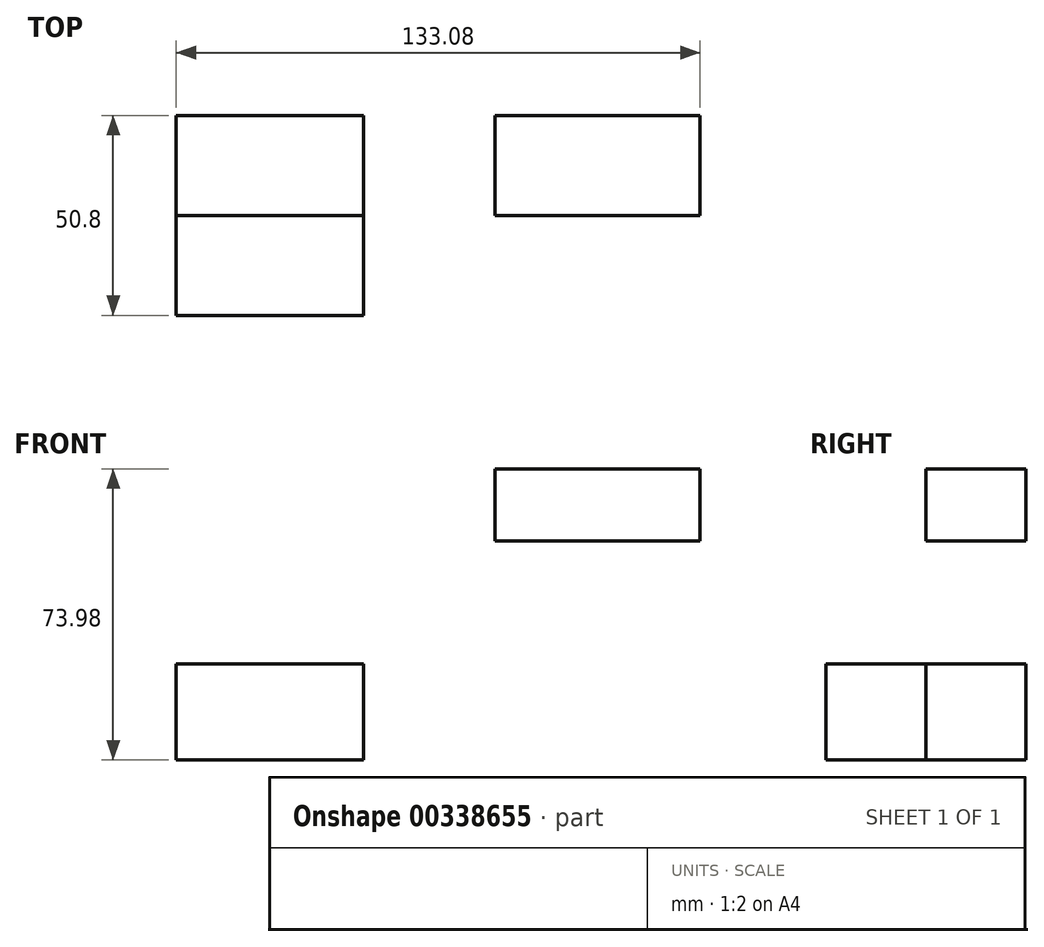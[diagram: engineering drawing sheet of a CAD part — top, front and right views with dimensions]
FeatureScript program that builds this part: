
annotation { "Feature Type Name" : "Feature", "Feature Type Description" : "" }
export const myFeature = defineFeature(function(context is Context, id is Id, definition is map)
    precondition{}
    {
        {
            var Q0;
            Q0=qCreatedBy(makeId("Front.planeOp"),FACE);
            var sketch = newSketch(context, id + "F0", { "sketchPlane" : qUnion([Q0])});
            skLineSegment(sketch, "E0.bottom", {"start": v(23.78, -12.24) * mm, "end": v(-23.78, -12.24) * mm});
            skLineSegment(sketch, "E0.top", {"start": v(23.78, 12.24) * mm, "end": v(-23.78, 12.24) * mm});
            skLineSegment(sketch, "E0.left", {"start": v(23.78, -12.24) * mm, "end": v(23.78, 12.24) * mm});
            skLineSegment(sketch, "E0.right", {"start": v(-23.78, -12.24) * mm, "end": v(-23.78, 12.24) * mm});
            skPoint(sketch, "E0.middle", {"position": v(0, 0) * mm});
            skLineSegment(sketch, "E1.bottom", {"start": v(109.3, 43.45) * mm, "end": v(57.17, 43.45) * mm});
            skLineSegment(sketch, "E1.top", {"start": v(109.3, 61.74) * mm, "end": v(57.17, 61.74) * mm});
            skLineSegment(sketch, "E1.left", {"start": v(109.3, 43.45) * mm, "end": v(109.3, 61.74) * mm});
            skPoint(sketch, "E1.middle", {"position": v(83.24, 52.6) * mm});
            skLineSegment(sketch, "E2", {"start": v(23.78, 12.24) * mm, "end": v(23.78, 43.45) * mm});
            skArc(sketch, "E3", {"start": v(23.78, 43.45) * mm, "mid": v(40.47, 60.14) * mm, "end": v(57.17, 43.45) * mm});
            skLineSegment(sketch, "E4", {"start": v(57.17, 61.74) * mm, "end": v(57.17, 43.45) * mm});
            skSolve(sketch);
        }
        {
            var Q0;
            Q0=makeQuery(id+"F0.imprint","IMPRINT",FACE,{"disambiguationData":[TD([[makeQuery(id+"F0.imprint","IMPRINT",EDGE,{"derivedFrom":sQuery(id+"F0.wireOp",EDGE,"E0.bottom")}),-1.0]])]});
            extrude(context, id + "F1", {"entities" : qUnion([Q0]), "depth" : 25.4 * mm});
        }
        {
            var Q0;
            Q0 = qSketchRegion(id + "F0", true);
            extrude(context, id + "F2", {"entities" : qUnion([Q0]), "oppositeDirection" : true, "depth" : 25.4 * mm});
        }
    });
